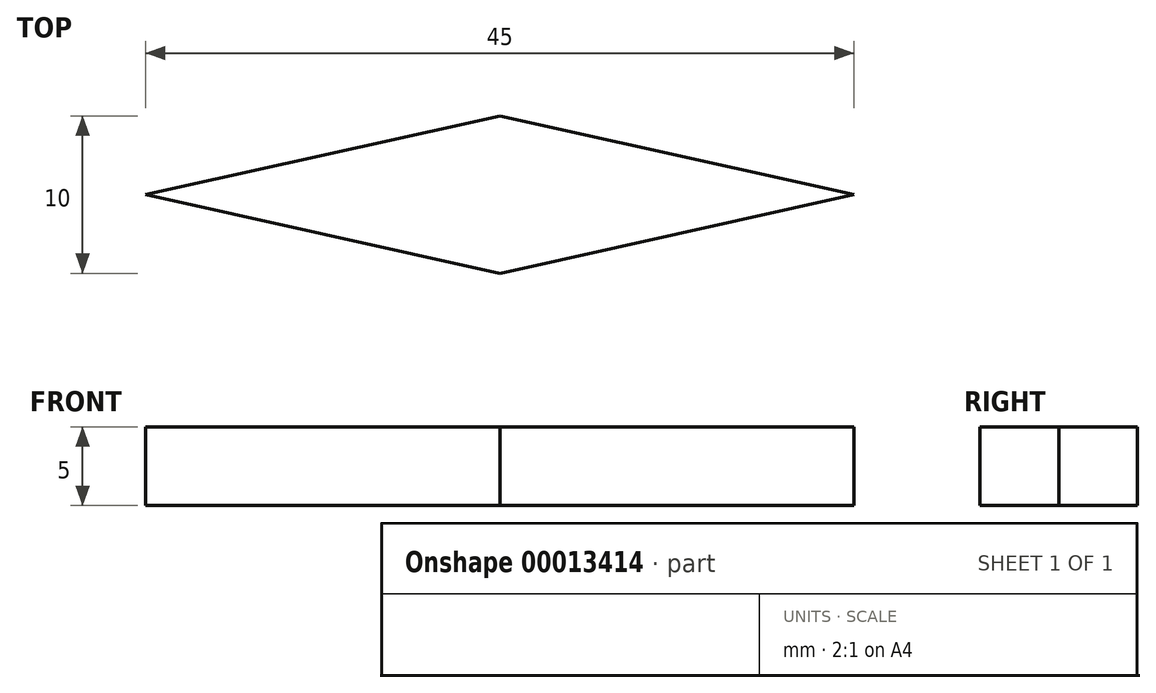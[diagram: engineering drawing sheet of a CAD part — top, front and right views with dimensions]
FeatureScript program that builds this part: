
annotation { "Feature Type Name" : "Feature", "Feature Type Description" : "" }
export const myFeature = defineFeature(function(context is Context, id is Id, definition is map)
    precondition{}
    {
        {
            var Q0;
            Q0=qCreatedBy(makeId("Top.planeOp"),FACE);
            var sketch = newSketch(context, id + "F0", { "sketchPlane" : qUnion([Q0])});
            skLineSegment(sketch, "E0.rect.bottom", {"start": v(-22.5, 5) * mm, "end": v(22.5, 5) * mm});
            skLineSegment(sketch, "E0.rect.top", {"start": v(-22.5, -5) * mm, "end": v(22.5, -5) * mm});
            skLineSegment(sketch, "E0.rect.left", {"start": v(-22.5, 5) * mm, "end": v(-22.5, -5) * mm});
            skLineSegment(sketch, "E0.rect.right", {"start": v(22.5, 5) * mm, "end": v(22.5, -5) * mm});
            skPoint(sketch, "E0.rect.middle", {"position": v(0, 0) * mm});
            skSolve(sketch);
        }
        {
            var Q0;
            Q0 = qSketchRegion(id + "F0", true);
            extrude(context, id + "F1", {"entities" : qUnion([Q0]), "depth" : 5 * mm});
        }
        {
            var Q0;
            Q0=makeQuery(id+"F1.opExtrude","CAP_FACE",FACE,{"disambiguationData":[OSD([sQuery(id+"F0.wireOp",EDGE,"E0.rect.bottom"),sQuery(id+"F0.wireOp",EDGE,"E0.rect.top"),sQuery(id+"F0.wireOp",EDGE,"E0.rect.left"),sQuery(id+"F0.wireOp",EDGE,"E0.rect.right")])],"isStart":true});
            var sketch = newSketch(context, id + "F2", { "sketchPlane" : qUnion([Q0])});
            skLineSegment(sketch, "E1", {"start": v(0, 5) * mm, "end": v(-22.5, 0) * mm});
            skLineSegment(sketch, "E2", {"start": v(-22.5, 0) * mm, "end": v(0, -5) * mm});
            skLineSegment(sketch, "E3", {"start": v(0, -5) * mm, "end": v(22.5, 0) * mm});
            skLineSegment(sketch, "E4", {"start": v(22.5, 0) * mm, "end": v(0, 5) * mm});
            skSolve(sketch);
        }
        {
            var Q0;
            Q0=makeQuery(id+"F2.imprint","IMPRINT",FACE,{"disambiguationData":[TD([[makeQuery(id+"F2.imprint","IMPRINT",EDGE,{"derivedFrom":sQuery(id+"F2.wireOp",EDGE,"E1")}),1.0]])]});
            extrude(context, id + "F3", {"entities" : qUnion([Q0]), "operationType" : NewBodyOperationType.INTERSECT, "endBound" : BoundingType.UP_TO_NEXT, "oppositeDirection" : true, "depth" : 25 * mm});
        }
    });
